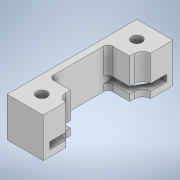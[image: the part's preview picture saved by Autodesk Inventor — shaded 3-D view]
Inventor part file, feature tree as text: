
AUTODESK INVENTOR PART (.ipt)
format: ipt  version: 2021.1 (Build 251245010, 245A)  size: 208,896 bytes
history: native  units: mm
features: extrude x4, sketch x4, other x1, fillet x1
ambient origin geometry x8: Origin, YZ Plane, XZ Plane, XY Plane, X Axis, Y Axis, Z Axis, Center Point
bodies: Body1 (feature_tree)
feature tree (10):
  other  "Твердое тело1"
  extrude  "Выдавливание1"  Depth=17.0mm
  extrude  "Выдавливание2"  Depth=17.0mm
  extrude  "Выдавливание3"  Depth=35.56mm
  fillet  "Сопряжение1"  Radius=2.0mm
  extrude  "Выдавливание4"  TaperAngle=90.0deg  [1 undecoded]
  sketch  "Эскиз1"
  sketch  "Эскиз2"
  sketch  "Эскиз3"
  sketch  "Эскиз4"
note: 1 required parameter value undecoded (feature->parameter linkage not recoverable at this tier; creation-order binding heuristic only, values carry confidence <= 0.55)
